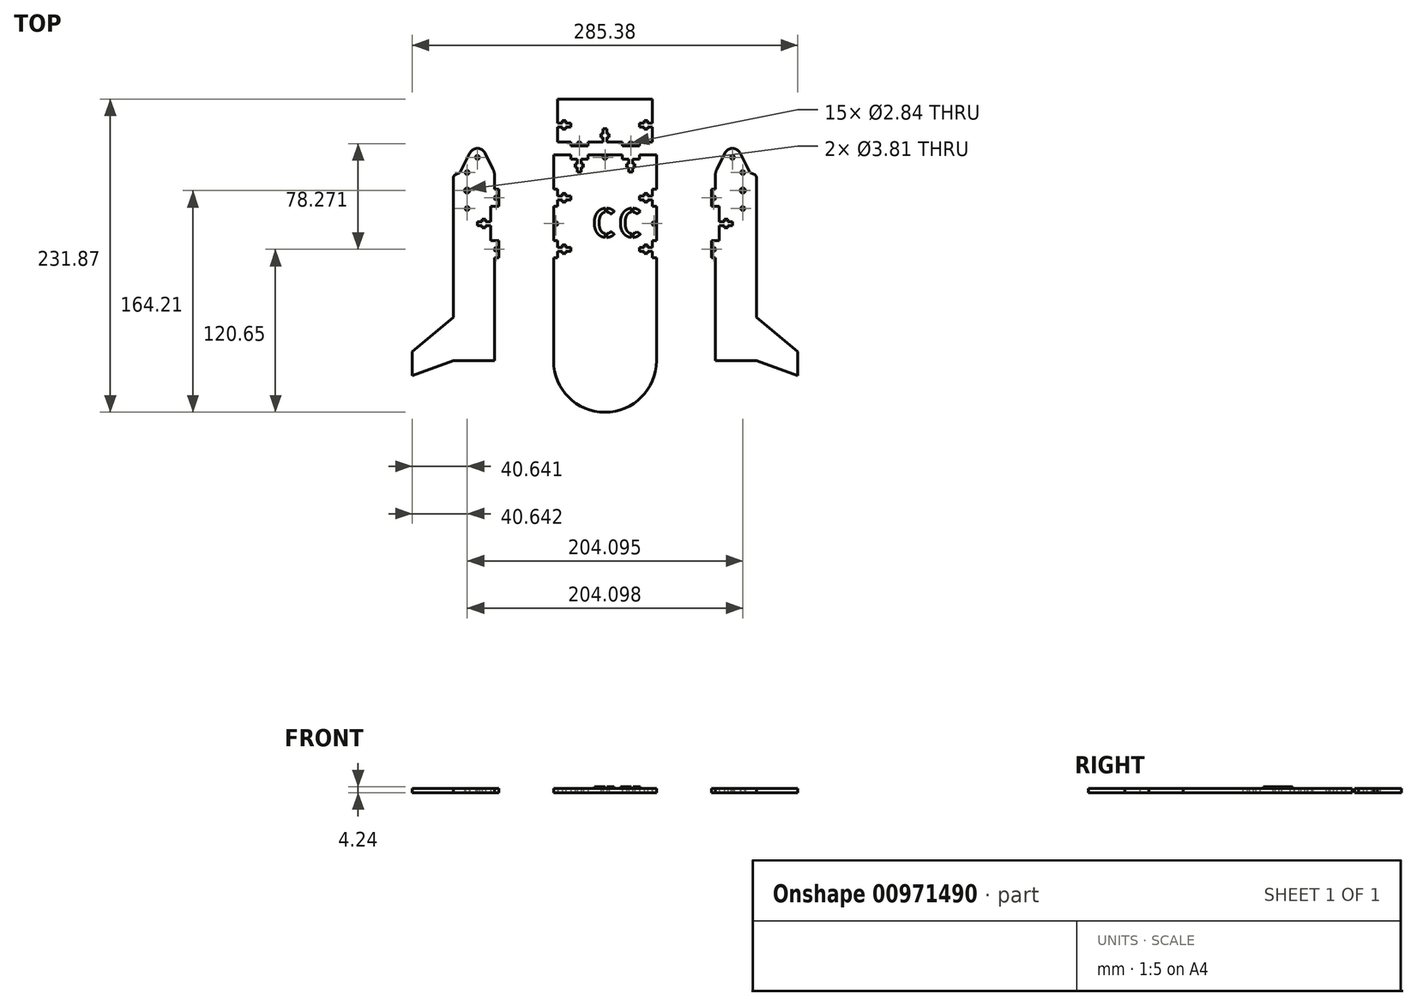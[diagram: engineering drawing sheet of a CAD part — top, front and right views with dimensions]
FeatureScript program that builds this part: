
annotation { "Feature Type Name" : "Feature", "Feature Type Description" : "" }
export const myFeature = defineFeature(function(context is Context, id is Id, definition is map)
    precondition{}
    {
        {
            var Q0;
            Q0=qCreatedBy(makeId("Top.planeOp"),FACE);
            var sketch = newSketch(context, id + "F0", { "sketchPlane" : qUnion([Q0])});
            skLineSegment(sketch, "E0", {"start": v(-12.7, 0) * mm, "end": v(12.7, 0) * mm});
            skLineSegment(sketch, "E1", {"start": v(-12.7, 0) * mm, "end": v(-12.7, -2.97) * mm});
            skLineSegment(sketch, "E2", {"start": v(-12.7, -2.97) * mm, "end": v(-17.63, -2.97) * mm});
            skLineSegment(sketch, "E3", {"start": v(-17.63, -9.1) * mm, "end": v(-17.63, -12.7) * mm});
            skLineSegment(sketch, "E4", {"start": v(-17.63, -12.7) * mm, "end": v(-20.47, -12.7) * mm});
            skLineSegment(sketch, "E5", {"start": v(-20.47, -12.7) * mm, "end": v(-20.47, -9.1) * mm});
            skLineSegment(sketch, "E6", {"start": v(-20.47, -6.57) * mm, "end": v(-20.47, -2.97) * mm});
            skLineSegment(sketch, "E7", {"start": v(-20.47, -2.97) * mm, "end": v(-25.4, -2.97) * mm});
            skLineSegment(sketch, "E8", {"start": v(-25.4, -2.97) * mm, "end": v(-25.4, 0) * mm});
            skCircle(sketch, "E9", {"center": v(0, -1.78) * mm, "radius": 1.42 * mm});
            skLineSegment(sketch, "E10", {"start": v(12.7, 0) * mm, "end": v(12.7, -2.97) * mm});
            skLineSegment(sketch, "E11", {"start": v(12.7, -2.97) * mm, "end": v(17.63, -2.97) * mm});
            skLineSegment(sketch, "E12", {"start": v(17.63, -2.97) * mm, "end": v(17.63, -6.57) * mm});
            skLineSegment(sketch, "E13", {"start": v(17.63, -9.1) * mm, "end": v(17.63, -12.7) * mm});
            skLineSegment(sketch, "E14", {"start": v(17.63, -12.7) * mm, "end": v(20.47, -12.7) * mm});
            skLineSegment(sketch, "E15", {"start": v(20.47, -12.7) * mm, "end": v(20.47, -9.1) * mm});
            skLineSegment(sketch, "E16", {"start": v(20.47, -6.57) * mm, "end": v(20.47, -2.97) * mm});
            skLineSegment(sketch, "E17", {"start": v(20.47, -2.97) * mm, "end": v(25.4, -2.97) * mm});
            skLineSegment(sketch, "E18", {"start": v(25.4, -2.97) * mm, "end": v(25.4, 0) * mm});
            skLineSegment(sketch, "E19", {"start": v(-38.1, 0) * mm, "end": v(-38.1, -25.4) * mm});
            skLineSegment(sketch, "E20", {"start": v(-38.1, -25.4) * mm, "end": v(-35.13, -25.4) * mm});
            skLineSegment(sketch, "E21", {"start": v(-35.13, -25.4) * mm, "end": v(-35.13, -30.33) * mm});
            skLineSegment(sketch, "E22", {"start": v(-35.13, -33.17) * mm, "end": v(-35.13, -38.1) * mm});
            skLineSegment(sketch, "E23", {"start": v(-35.13, -38.1) * mm, "end": v(-38.1, -38.1) * mm});
            skLineSegment(sketch, "E24", {"start": v(-25.4, 0) * mm, "end": v(-38.1, 0) * mm});
            skLineSegment(sketch, "E25", {"start": v(-20.47, -6.57) * mm, "end": v(-22.2, -6.57) * mm});
            skLineSegment(sketch, "E26", {"start": v(-22.2, -6.57) * mm, "end": v(-22.2, -9.1) * mm});
            skLineSegment(sketch, "E27", {"start": v(-22.2, -9.1) * mm, "end": v(-20.47, -9.1) * mm});
            skLineSegment(sketch, "E28", {"start": v(-17.63, -9.1) * mm, "end": v(-15.9, -9.1) * mm});
            skLineSegment(sketch, "E29", {"start": v(-15.9, -9.1) * mm, "end": v(-15.9, -6.57) * mm});
            skLineSegment(sketch, "E30", {"start": v(-15.9, -6.57) * mm, "end": v(-17.63, -6.57) * mm});
            skLineSegment(sketch, "E31", {"start": v(17.63, -6.57) * mm, "end": v(15.9, -6.57) * mm});
            skLineSegment(sketch, "E32", {"start": v(15.9, -6.57) * mm, "end": v(15.9, -9.1) * mm});
            skLineSegment(sketch, "E33", {"start": v(15.9, -9.1) * mm, "end": v(17.63, -9.1) * mm});
            skLineSegment(sketch, "E34", {"start": v(20.47, -9.1) * mm, "end": v(22.2, -9.1) * mm});
            skLineSegment(sketch, "E35", {"start": v(22.2, -9.1) * mm, "end": v(22.2, -6.57) * mm});
            skLineSegment(sketch, "E36", {"start": v(22.2, -6.57) * mm, "end": v(20.47, -6.57) * mm});
            skLineSegment(sketch, "E37", {"start": v(0, 0) * mm, "end": v(-12.7, 0) * mm, "construction": true});
            skLineSegment(sketch, "E38", {"start": v(0, 0) * mm, "end": v(12.7, 0) * mm, "construction": true});
            skLineSegment(sketch, "E39", {"start": v(-17.63, -6.57) * mm, "end": v(-17.63, -2.97) * mm});
            skLineSegment(sketch, "E40", {"start": v(-35.13, -30.33) * mm, "end": v(-31.53, -30.33) * mm});
            skLineSegment(sketch, "E41", {"start": v(-31.53, -30.33) * mm, "end": v(-31.53, -28.6) * mm});
            skLineSegment(sketch, "E42", {"start": v(-31.53, -28.6) * mm, "end": v(-29, -28.6) * mm});
            skLineSegment(sketch, "E43", {"start": v(-29, -28.6) * mm, "end": v(-29, -30.33) * mm});
            skLineSegment(sketch, "E44", {"start": v(-29, -30.33) * mm, "end": v(-25.4, -30.33) * mm});
            skLineSegment(sketch, "E45", {"start": v(-25.4, -30.33) * mm, "end": v(-25.4, -33.17) * mm});
            skLineSegment(sketch, "E46", {"start": v(-25.4, -33.17) * mm, "end": v(-29, -33.17) * mm});
            skLineSegment(sketch, "E47", {"start": v(-29, -33.17) * mm, "end": v(-29, -34.9) * mm});
            skLineSegment(sketch, "E48", {"start": v(-29, -34.9) * mm, "end": v(-31.53, -34.9) * mm});
            skLineSegment(sketch, "E49", {"start": v(-31.53, -34.9) * mm, "end": v(-31.53, -33.17) * mm});
            skLineSegment(sketch, "E50", {"start": v(-31.53, -33.17) * mm, "end": v(-35.13, -33.17) * mm});
            skLineSegment(sketch, "E51", {"start": v(-38.1, -38.1) * mm, "end": v(-38.1, -63.5) * mm});
            skCircle(sketch, "E52", {"center": v(-36.32, -50.8) * mm, "radius": 1.42 * mm});
            skLineSegment(sketch, "E53", {"start": v(-38.1, -63.5) * mm, "end": v(-35.13, -63.5) * mm});
            skLineSegment(sketch, "E54", {"start": v(-35.13, -63.5) * mm, "end": v(-35.13, -68.43) * mm});
            skLineSegment(sketch, "E55", {"start": v(-35.13, -68.43) * mm, "end": v(-31.53, -68.43) * mm});
            skLineSegment(sketch, "E56", {"start": v(-31.53, -68.43) * mm, "end": v(-31.53, -66.7) * mm});
            skLineSegment(sketch, "E57", {"start": v(-31.53, -66.7) * mm, "end": v(-29, -66.7) * mm});
            skLineSegment(sketch, "E58", {"start": v(-29, -66.7) * mm, "end": v(-29, -68.43) * mm});
            skLineSegment(sketch, "E59", {"start": v(-29, -68.43) * mm, "end": v(-25.4, -68.43) * mm});
            skLineSegment(sketch, "E60", {"start": v(-25.4, -68.43) * mm, "end": v(-25.4, -71.27) * mm});
            skLineSegment(sketch, "E61", {"start": v(-25.4, -71.27) * mm, "end": v(-29, -71.27) * mm});
            skLineSegment(sketch, "E62", {"start": v(-29, -71.27) * mm, "end": v(-29, -73) * mm});
            skLineSegment(sketch, "E63", {"start": v(-29, -73) * mm, "end": v(-31.53, -73) * mm});
            skLineSegment(sketch, "E64", {"start": v(-31.53, -73) * mm, "end": v(-31.53, -71.27) * mm});
            skLineSegment(sketch, "E65", {"start": v(-31.53, -71.27) * mm, "end": v(-35.13, -71.27) * mm});
            skLineSegment(sketch, "E66", {"start": v(-35.13, -71.27) * mm, "end": v(-35.13, -76.2) * mm});
            skLineSegment(sketch, "E67", {"start": v(-35.13, -76.2) * mm, "end": v(-38.1, -76.2) * mm});
            skLineSegment(sketch, "E68", {"start": v(-38.1, -76.2) * mm, "end": v(-38.1, -152.4) * mm});
            skLineSegment(sketch, "E69", {"start": v(0, -190.5) * mm, "end": v(0, -190.5) * mm});
            skPoint(sketch, "E70.visualSharp", {"position": v(-38.1, -190.5) * mm});
            skArc(sketch, "E70.filletArc", {"start": v(-38.1, -152.4) * mm, "mid": v(-26.94, -179.34) * mm, "end": v(0, -190.5) * mm});
            skPoint(sketch, "E71.visualSharp", {"position": v(38.1, -190.5) * mm});
            skLineSegment(sketch, "E72", {"start": v(0, -190.5) * mm, "end": v(0, -135.08) * mm, "construction": true});
            skArc(sketch, "E73.MirrorCS", {"start": v(38.1, -152.4) * mm, "mid": v(26.94, -179.34) * mm, "end": v(0, -190.5) * mm});
            skLineSegment(sketch, "E74.MirrorCS", {"start": v(38.1, -76.2) * mm, "end": v(38.1, -152.4) * mm});
            skLineSegment(sketch, "E75.MirrorCS", {"start": v(35.13, -76.2) * mm, "end": v(38.1, -76.2) * mm});
            skLineSegment(sketch, "E76.MirrorCS", {"start": v(35.13, -71.27) * mm, "end": v(35.13, -76.2) * mm});
            skLineSegment(sketch, "E77.MirrorCS", {"start": v(31.53, -71.27) * mm, "end": v(35.13, -71.27) * mm});
            skLineSegment(sketch, "E78.MirrorCS", {"start": v(31.53, -73) * mm, "end": v(31.53, -71.27) * mm});
            skLineSegment(sketch, "E79.MirrorCS", {"start": v(29, -73) * mm, "end": v(31.53, -73) * mm});
            skLineSegment(sketch, "E80.MirrorCS", {"start": v(29, -71.27) * mm, "end": v(29, -73) * mm});
            skLineSegment(sketch, "E81.MirrorCS", {"start": v(25.4, -71.27) * mm, "end": v(29, -71.27) * mm});
            skLineSegment(sketch, "E82.MirrorCS", {"start": v(25.4, -68.43) * mm, "end": v(25.4, -71.27) * mm});
            skLineSegment(sketch, "E83.MirrorCS", {"start": v(29, -68.43) * mm, "end": v(25.4, -68.43) * mm});
            skLineSegment(sketch, "E84.MirrorCS", {"start": v(29, -66.7) * mm, "end": v(29, -68.43) * mm});
            skLineSegment(sketch, "E85.MirrorCS", {"start": v(31.53, -66.7) * mm, "end": v(29, -66.7) * mm});
            skLineSegment(sketch, "E86.MirrorCS", {"start": v(31.53, -68.43) * mm, "end": v(31.53, -66.7) * mm});
            skLineSegment(sketch, "E87.MirrorCS", {"start": v(35.13, -68.43) * mm, "end": v(31.53, -68.43) * mm});
            skLineSegment(sketch, "E88.MirrorCS", {"start": v(35.13, -63.5) * mm, "end": v(35.13, -68.43) * mm});
            skLineSegment(sketch, "E89.MirrorCS", {"start": v(38.1, -63.5) * mm, "end": v(35.13, -63.5) * mm});
            skLineSegment(sketch, "E90.MirrorCS", {"start": v(38.1, -38.1) * mm, "end": v(38.1, -63.5) * mm});
            skCircle(sketch, "E91.MirrorC", {"center": v(36.32, -50.8) * mm, "radius": 1.42 * mm});
            skLineSegment(sketch, "E92.MirrorCS", {"start": v(35.13, -38.1) * mm, "end": v(38.1, -38.1) * mm});
            skLineSegment(sketch, "E93.MirrorCS", {"start": v(35.13, -33.17) * mm, "end": v(35.13, -38.1) * mm});
            skLineSegment(sketch, "E94.MirrorCS", {"start": v(31.53, -33.17) * mm, "end": v(35.13, -33.17) * mm});
            skLineSegment(sketch, "E95.MirrorCS", {"start": v(31.53, -34.9) * mm, "end": v(31.53, -33.17) * mm});
            skLineSegment(sketch, "E96.MirrorCS", {"start": v(29, -34.9) * mm, "end": v(31.53, -34.9) * mm});
            skLineSegment(sketch, "E97.MirrorCS", {"start": v(29, -33.17) * mm, "end": v(29, -34.9) * mm});
            skLineSegment(sketch, "E98.MirrorCS", {"start": v(25.4, -33.17) * mm, "end": v(29, -33.17) * mm});
            skLineSegment(sketch, "E99.MirrorCS", {"start": v(25.4, -30.33) * mm, "end": v(25.4, -33.17) * mm});
            skLineSegment(sketch, "E100.MirrorCS", {"start": v(29, -30.33) * mm, "end": v(25.4, -30.33) * mm});
            skLineSegment(sketch, "E101.MirrorCS", {"start": v(29, -28.6) * mm, "end": v(29, -30.33) * mm});
            skLineSegment(sketch, "E102.MirrorCS", {"start": v(31.53, -28.6) * mm, "end": v(29, -28.6) * mm});
            skLineSegment(sketch, "E103.MirrorCS", {"start": v(31.53, -30.33) * mm, "end": v(31.53, -28.6) * mm});
            skLineSegment(sketch, "E104.MirrorCS", {"start": v(35.13, -30.33) * mm, "end": v(31.53, -30.33) * mm});
            skLineSegment(sketch, "E105.MirrorCS", {"start": v(35.13, -25.4) * mm, "end": v(35.13, -30.33) * mm});
            skLineSegment(sketch, "E106.MirrorCS", {"start": v(38.1, -25.4) * mm, "end": v(35.13, -25.4) * mm});
            skLineSegment(sketch, "E107.MirrorCS", {"start": v(38.1, 0) * mm, "end": v(38.1, -25.4) * mm});
            skLineSegment(sketch, "E108.MirrorCS", {"start": v(25.4, 0) * mm, "end": v(38.1, 0) * mm});
            skLineSegment(sketch, "E109", {"start": v(-12.7, 0) * mm, "end": v(-12.7, 6.64) * mm, "construction": true});
            skLineSegment(sketch, "E110", {"start": v(-12.7, 6.64) * mm, "end": v(-12.7, 9.62) * mm});
            skLineSegment(sketch, "E111", {"start": v(-12.7, 9.62) * mm, "end": v(-1.42, 9.62) * mm});
            skLineSegment(sketch, "E112.MirrorCS", {"start": v(12.7, 9.62) * mm, "end": v(1.42, 9.62) * mm});
            skLineSegment(sketch, "E113.MirrorCS", {"start": v(12.7, 6.64) * mm, "end": v(12.7, 9.62) * mm});
            skLineSegment(sketch, "E114", {"start": v(-1.42, 9.62) * mm, "end": v(-1.42, 13.2) * mm});
            skLineSegment(sketch, "E115", {"start": v(-1.42, 13.2) * mm, "end": v(-3.15, 13.2) * mm});
            skLineSegment(sketch, "E116", {"start": v(-3.15, 13.2) * mm, "end": v(-3.15, 15.75) * mm});
            skLineSegment(sketch, "E117", {"start": v(-3.15, 15.75) * mm, "end": v(-1.42, 15.75) * mm});
            skLineSegment(sketch, "E118", {"start": v(-1.42, 15.75) * mm, "end": v(-1.42, 19.34) * mm});
            skLineSegment(sketch, "E119.MirrorCS", {"start": v(1.42, 9.62) * mm, "end": v(1.42, 13.2) * mm});
            skLineSegment(sketch, "E120.MirrorCS", {"start": v(1.42, 13.2) * mm, "end": v(3.15, 13.2) * mm});
            skLineSegment(sketch, "E121.MirrorCS", {"start": v(3.15, 13.2) * mm, "end": v(3.15, 15.75) * mm});
            skLineSegment(sketch, "E122.MirrorCS", {"start": v(3.15, 15.75) * mm, "end": v(1.42, 15.75) * mm});
            skLineSegment(sketch, "E123.MirrorCS", {"start": v(1.42, 15.75) * mm, "end": v(1.42, 19.34) * mm});
            skLineSegment(sketch, "E124", {"start": v(-1.42, 19.34) * mm, "end": v(1.42, 19.34) * mm});
            skLineSegment(sketch, "E125", {"start": v(12.7, 6.64) * mm, "end": v(25.4, 6.64) * mm});
            skLineSegment(sketch, "E126", {"start": v(-12.7, 6.64) * mm, "end": v(-25.4, 6.64) * mm});
            skCircle(sketch, "E127", {"center": v(-19.05, 8.42) * mm, "radius": 1.42 * mm});
            skLineSegment(sketch, "E128", {"start": v(25.4, 6.64) * mm, "end": v(25.4, 9.62) * mm});
            skCircle(sketch, "E129.MirrorC", {"center": v(19.05, 8.42) * mm, "radius": 1.42 * mm});
            skLineSegment(sketch, "E130.MirrorCS", {"start": v(-25.4, 6.64) * mm, "end": v(-25.4, 9.62) * mm});
            skLineSegment(sketch, "E131", {"start": v(35.13, 20.9) * mm, "end": v(31.53, 20.9) * mm});
            skLineSegment(sketch, "E132", {"start": v(31.53, 20.9) * mm, "end": v(31.53, 19.17) * mm});
            skLineSegment(sketch, "E133", {"start": v(31.53, 19.17) * mm, "end": v(29, 19.17) * mm});
            skLineSegment(sketch, "E134", {"start": v(29, 19.17) * mm, "end": v(29, 20.9) * mm});
            skLineSegment(sketch, "E135", {"start": v(29, 20.9) * mm, "end": v(25.4, 20.9) * mm});
            skLineSegment(sketch, "E136", {"start": v(25.4, 20.9) * mm, "end": v(25.4, 23.74) * mm});
            skLineSegment(sketch, "E137", {"start": v(25.4, 23.74) * mm, "end": v(29, 23.74) * mm});
            skLineSegment(sketch, "E138", {"start": v(29, 23.74) * mm, "end": v(29, 25.46) * mm});
            skLineSegment(sketch, "E139", {"start": v(29, 25.46) * mm, "end": v(31.53, 25.46) * mm});
            skLineSegment(sketch, "E140", {"start": v(31.53, 25.46) * mm, "end": v(31.53, 23.74) * mm});
            skLineSegment(sketch, "E141", {"start": v(31.53, 23.74) * mm, "end": v(35.13, 23.74) * mm});
            skLineSegment(sketch, "E142.MirrorCS", {"start": v(-35.13, 20.9) * mm, "end": v(-31.53, 20.9) * mm});
            skLineSegment(sketch, "E143.MirrorCS", {"start": v(-31.53, 20.9) * mm, "end": v(-31.53, 19.17) * mm});
            skLineSegment(sketch, "E144.MirrorCS", {"start": v(-31.53, 19.17) * mm, "end": v(-29, 19.17) * mm});
            skLineSegment(sketch, "E145.MirrorCS", {"start": v(-29, 19.17) * mm, "end": v(-29, 20.9) * mm});
            skLineSegment(sketch, "E146.MirrorCS", {"start": v(-29, 20.9) * mm, "end": v(-25.4, 20.9) * mm});
            skLineSegment(sketch, "E147.MirrorCS", {"start": v(-25.4, 20.9) * mm, "end": v(-25.4, 23.74) * mm});
            skLineSegment(sketch, "E148.MirrorCS", {"start": v(-25.4, 23.74) * mm, "end": v(-29, 23.74) * mm});
            skLineSegment(sketch, "E149.MirrorCS", {"start": v(-29, 23.74) * mm, "end": v(-29, 25.46) * mm});
            skLineSegment(sketch, "E150.MirrorCS", {"start": v(-29, 25.46) * mm, "end": v(-31.53, 25.46) * mm});
            skLineSegment(sketch, "E151.MirrorCS", {"start": v(-31.53, 25.46) * mm, "end": v(-31.53, 23.74) * mm});
            skLineSegment(sketch, "E152.MirrorCS", {"start": v(-31.53, 23.74) * mm, "end": v(-35.13, 23.74) * mm});
            skLineSegment(sketch, "E153", {"start": v(-38.1, 0) * mm, "end": v(-81.73, 0) * mm, "construction": true});
            skLineSegment(sketch, "E154", {"start": v(-81.73, 0) * mm, "end": v(-81.73, -12.7) * mm, "construction": true});
            skLineSegment(sketch, "E155", {"start": v(-81.73, -15.4) * mm, "end": v(-81.73, -25.36) * mm});
            skLineSegment(sketch, "E156", {"start": v(-82.94, -10.29) * mm, "end": v(-88.75, 1.34) * mm});
            skLineSegment(sketch, "E157", {"start": v(-100.1, 1.34) * mm, "end": v(-106.75, -11.94) * mm});
            skPoint(sketch, "E158.visualSharp", {"position": v(-81.73, -12.7) * mm});
            skArc(sketch, "E158.filletArc", {"start": v(-81.73, -15.4) * mm, "mid": v(-82.03, -12.77) * mm, "end": v(-82.94, -10.29) * mm});
            skPoint(sketch, "E159.visualSharp", {"position": v(-94.43, 12.7) * mm});
            skArc(sketch, "E159.filletArc", {"start": v(-88.75, 1.34) * mm, "mid": v(-94.43, 4.85) * mm, "end": v(-100.1, 1.34) * mm});
            skLineSegment(sketch, "E160", {"start": v(-107.89, -13.08) * mm, "end": v(-110.8, -14.54) * mm});
            skPoint(sketch, "E161.visualSharp", {"position": v(-107.13, -12.7) * mm});
            skArc(sketch, "E161.filletArc", {"start": v(-107.89, -13.08) * mm, "mid": v(-107.23, -12.6) * mm, "end": v(-106.75, -11.94) * mm});
            skLineSegment(sketch, "E162", {"start": v(-112.2, -16.8) * mm, "end": v(-112.2, -120.14) * mm});
            skPoint(sketch, "E163.visualSharp", {"position": v(-112.2, -15.24) * mm});
            skArc(sketch, "E163.filletArc", {"start": v(-110.8, -14.54) * mm, "mid": v(-111.83, -15.47) * mm, "end": v(-112.2, -16.8) * mm});
            skLineSegment(sketch, "E164", {"start": v(-112.2, -152.4) * mm, "end": v(-81.73, -152.4) * mm});
            skLineSegment(sketch, "E165", {"start": v(-112.2, -152.4) * mm, "end": v(-142.69, -163.5) * mm});
            skLineSegment(sketch, "E166", {"start": v(-142.69, -163.5) * mm, "end": v(-142.69, -145.71) * mm});
            skLineSegment(sketch, "E167", {"start": v(-142.69, -145.71) * mm, "end": v(-112.2, -120.14) * mm});
            skLineSegment(sketch, "E168", {"start": v(-81.73, 0) * mm, "end": v(-94.43, 0) * mm, "construction": true});
            skCircle(sketch, "E169", {"center": v(-94.43, -1.78) * mm, "radius": 1.42 * mm});
            skCircle(sketch, "E170", {"center": v(-80.54, -31.75) * mm, "radius": 1.42 * mm});
            skLineSegment(sketch, "E171", {"start": v(-81.73, -38.1) * mm, "end": v(-84.7, -38.1) * mm});
            skLineSegment(sketch, "E172", {"start": v(-84.7, -38.1) * mm, "end": v(-84.7, -49.38) * mm});
            skLineSegment(sketch, "E173", {"start": v(-84.7, -49.38) * mm, "end": v(-88.3, -49.38) * mm});
            skLineSegment(sketch, "E174", {"start": v(-88.3, -49.38) * mm, "end": v(-88.3, -47.65) * mm});
            skLineSegment(sketch, "E175", {"start": v(-88.3, -47.65) * mm, "end": v(-90.84, -47.65) * mm});
            skLineSegment(sketch, "E176", {"start": v(-90.84, -47.65) * mm, "end": v(-90.84, -49.38) * mm});
            skLineSegment(sketch, "E177", {"start": v(-90.84, -49.38) * mm, "end": v(-94.43, -49.38) * mm});
            skLineSegment(sketch, "E178", {"start": v(-94.43, -49.38) * mm, "end": v(-94.43, -52.22) * mm});
            skLineSegment(sketch, "E179", {"start": v(-94.43, -52.22) * mm, "end": v(-90.84, -52.22) * mm});
            skLineSegment(sketch, "E180", {"start": v(-90.84, -52.22) * mm, "end": v(-90.84, -53.95) * mm});
            skLineSegment(sketch, "E181", {"start": v(-90.84, -53.95) * mm, "end": v(-88.3, -53.95) * mm});
            skLineSegment(sketch, "E182", {"start": v(-88.3, -53.95) * mm, "end": v(-88.3, -52.22) * mm});
            skLineSegment(sketch, "E183", {"start": v(-88.3, -52.22) * mm, "end": v(-84.7, -52.22) * mm});
            skLineSegment(sketch, "E184", {"start": v(-84.7, -52.22) * mm, "end": v(-84.7, -63.5) * mm});
            skLineSegment(sketch, "E185", {"start": v(-84.7, -63.5) * mm, "end": v(-81.73, -63.5) * mm});
            skLineSegment(sketch, "E186.trimOffspring", {"start": v(-81.73, -76.2) * mm, "end": v(-81.73, -152.4) * mm});
            skCircle(sketch, "E187", {"center": v(-80.54, -69.85) * mm, "radius": 1.42 * mm});
            skCircle(sketch, "E188", {"center": v(-102.05, -12.96) * mm, "radius": 1.42 * mm});
            skCircle(sketch, "E189", {"center": v(-102.05, -26.3) * mm, "radius": 1.9 * mm});
            skLineSegment(sketch, "E190", {"start": v(-102.05, -12.96) * mm, "end": v(-81.73, -12.7) * mm, "construction": true});
            skLineSegment(sketch, "E191", {"start": v(-102.05, -26.3) * mm, "end": v(-81.73, -26.3) * mm, "construction": true});
            skCircle(sketch, "E192.MirrorC", {"center": v(-102.05, -39.63) * mm, "radius": 1.42 * mm});
            skLineSegment(sketch, "E193.MirrorCS", {"start": v(81.73, -76.2) * mm, "end": v(81.73, -152.4) * mm});
            skLineSegment(sketch, "E194.MirrorCS", {"start": v(112.2, -152.4) * mm, "end": v(81.73, -152.4) * mm});
            skLineSegment(sketch, "E195.MirrorCS", {"start": v(112.2, -152.4) * mm, "end": v(142.69, -163.5) * mm});
            skLineSegment(sketch, "E196.MirrorCS", {"start": v(142.69, -163.5) * mm, "end": v(142.69, -145.71) * mm});
            skLineSegment(sketch, "E197.MirrorCS", {"start": v(142.69, -145.71) * mm, "end": v(112.2, -120.14) * mm});
            skLineSegment(sketch, "E198.MirrorCS", {"start": v(112.2, -16.8) * mm, "end": v(112.2, -120.14) * mm});
            skArc(sketch, "E199.MirrorCS", {"start": v(110.8, -14.54) * mm, "mid": v(111.83, -15.47) * mm, "end": v(112.2, -16.8) * mm});
            skLineSegment(sketch, "E200.MirrorCS", {"start": v(107.89, -13.08) * mm, "end": v(110.8, -14.54) * mm});
            skArc(sketch, "E201.MirrorCS", {"start": v(107.89, -13.08) * mm, "mid": v(107.23, -12.6) * mm, "end": v(106.75, -11.94) * mm});
            skLineSegment(sketch, "E202.MirrorCS", {"start": v(100.1, 1.34) * mm, "end": v(106.75, -11.94) * mm});
            skArc(sketch, "E203.MirrorCS", {"start": v(88.75, 1.34) * mm, "mid": v(94.43, 4.85) * mm, "end": v(100.1, 1.34) * mm});
            skLineSegment(sketch, "E204.MirrorCS", {"start": v(82.94, -10.29) * mm, "end": v(88.75, 1.34) * mm});
            skArc(sketch, "E205.MirrorCS", {"start": v(81.73, -15.4) * mm, "mid": v(82.03, -12.77) * mm, "end": v(82.94, -10.29) * mm});
            skLineSegment(sketch, "E206.MirrorCS", {"start": v(81.73, -15.4) * mm, "end": v(81.73, -25.36) * mm});
            skCircle(sketch, "E207.MirrorC", {"center": v(80.54, -69.85) * mm, "radius": 1.42 * mm});
            skCircle(sketch, "E208.MirrorC", {"center": v(80.54, -31.75) * mm, "radius": 1.42 * mm});
            skLineSegment(sketch, "E209.MirrorCS", {"start": v(81.73, -38.1) * mm, "end": v(84.7, -38.1) * mm});
            skLineSegment(sketch, "E210.MirrorCS", {"start": v(84.7, -38.1) * mm, "end": v(84.7, -49.38) * mm});
            skLineSegment(sketch, "E211.MirrorCS", {"start": v(84.7, -52.22) * mm, "end": v(84.7, -63.5) * mm});
            skLineSegment(sketch, "E212.MirrorCS", {"start": v(84.7, -63.5) * mm, "end": v(81.73, -63.5) * mm});
            skLineSegment(sketch, "E213.MirrorCS", {"start": v(88.3, -52.22) * mm, "end": v(84.7, -52.22) * mm});
            skLineSegment(sketch, "E214.MirrorCS", {"start": v(84.7, -49.38) * mm, "end": v(88.3, -49.38) * mm});
            skLineSegment(sketch, "E215.MirrorCS", {"start": v(88.3, -49.38) * mm, "end": v(88.3, -47.65) * mm});
            skLineSegment(sketch, "E216.MirrorCS", {"start": v(88.3, -47.65) * mm, "end": v(90.84, -47.65) * mm});
            skLineSegment(sketch, "E217.MirrorCS", {"start": v(90.84, -47.65) * mm, "end": v(90.84, -49.38) * mm});
            skLineSegment(sketch, "E218.MirrorCS", {"start": v(90.84, -49.38) * mm, "end": v(94.43, -49.38) * mm});
            skLineSegment(sketch, "E219.MirrorCS", {"start": v(94.43, -49.38) * mm, "end": v(94.43, -52.22) * mm});
            skLineSegment(sketch, "E220.MirrorCS", {"start": v(94.43, -52.22) * mm, "end": v(90.84, -52.22) * mm});
            skLineSegment(sketch, "E221.MirrorCS", {"start": v(90.84, -52.22) * mm, "end": v(90.84, -53.95) * mm});
            skLineSegment(sketch, "E222.MirrorCS", {"start": v(90.84, -53.95) * mm, "end": v(88.3, -53.95) * mm});
            skLineSegment(sketch, "E223.MirrorCS", {"start": v(88.3, -53.95) * mm, "end": v(88.3, -52.22) * mm});
            skCircle(sketch, "E224.MirrorC", {"center": v(94.43, -1.78) * mm, "radius": 1.42 * mm});
            skCircle(sketch, "E225.MirrorC", {"center": v(102.05, -12.96) * mm, "radius": 1.42 * mm});
            skCircle(sketch, "E226.MirrorC", {"center": v(102.05, -26.3) * mm, "radius": 1.9 * mm});
            skCircle(sketch, "E227.MirrorC", {"center": v(102.05, -39.63) * mm, "radius": 1.42 * mm});
            skLineSegment(sketch, "E228", {"start": v(-25.4, 9.62) * mm, "end": v(-35.13, 9.62) * mm});
            skLineSegment(sketch, "E229", {"start": v(-35.13, 9.62) * mm, "end": v(-35.13, 20.9) * mm});
            skLineSegment(sketch, "E230", {"start": v(25.4, 9.62) * mm, "end": v(35.13, 9.62) * mm});
            skLineSegment(sketch, "E231", {"start": v(35.13, 9.62) * mm, "end": v(35.13, 20.9) * mm});
            skLineSegment(sketch, "E232", {"start": v(-35.13, 23.74) * mm, "end": v(-35.13, 41.37) * mm});
            skLineSegment(sketch, "E233", {"start": v(35.13, 23.74) * mm, "end": v(35.13, 41.37) * mm});
            skLineSegment(sketch, "E234", {"start": v(-35.13, 41.37) * mm, "end": v(35.13, 41.37) * mm});
            skLineSegment(sketch, "E235", {"start": v(-81.73, -38.1) * mm, "end": v(-78.76, -38.06) * mm});
            skLineSegment(sketch, "E236", {"start": v(-78.76, -38.06) * mm, "end": v(-78.76, -25.36) * mm});
            skLineSegment(sketch, "E237", {"start": v(-78.76, -25.36) * mm, "end": v(-81.73, -25.36) * mm});
            skLineSegment(sketch, "E238", {"start": v(-81.73, -63.5) * mm, "end": v(-78.76, -63.5) * mm});
            skLineSegment(sketch, "E239", {"start": v(-78.76, -63.5) * mm, "end": v(-78.76, -76.2) * mm});
            skLineSegment(sketch, "E240", {"start": v(-78.76, -76.2) * mm, "end": v(-81.73, -76.2) * mm});
            skLineSegment(sketch, "E241.MirrorCS", {"start": v(78.76, -25.36) * mm, "end": v(81.73, -25.36) * mm});
            skLineSegment(sketch, "E242.MirrorCS", {"start": v(78.76, -38.06) * mm, "end": v(78.76, -25.36) * mm});
            skLineSegment(sketch, "E243.MirrorCS", {"start": v(81.73, -38.1) * mm, "end": v(78.76, -38.06) * mm});
            skLineSegment(sketch, "E244.MirrorCS", {"start": v(81.73, -63.5) * mm, "end": v(78.76, -63.5) * mm});
            skLineSegment(sketch, "E245.MirrorCS", {"start": v(78.76, -63.5) * mm, "end": v(78.76, -76.2) * mm});
            skLineSegment(sketch, "E246.MirrorCS", {"start": v(78.76, -76.2) * mm, "end": v(81.73, -76.2) * mm});
            skPoint(sketch, "E247.trimOffspring.end.orphan", {"position": v(81.73, -38.1) * mm});
            skPoint(sketch, "E248.orphan", {"position": v(81.73, -63.5) * mm});
            skSolve(sketch);
        }
        {
            var Q0;
            Q0 = qSketchRegion(id + "F0", true);
            extrude(context, id + "F1", {"entities" : qUnion([Q0]), "depth" : 2.97 * mm, "offsetDistance" : 25.4 * mm});
        }
        {
            var Q0;
            Q0=makeQuery(id+"F1.opExtrude","CAP_FACE",FACE,{"disambiguationData":[OSD([sQuery(id+"F0.wireOp",EDGE,"E0"),sQuery(id+"F0.wireOp",EDGE,"E1"),sQuery(id+"F0.wireOp",EDGE,"E2"),sQuery(id+"F0.wireOp",EDGE,"E3"),sQuery(id+"F0.wireOp",EDGE,"E4"),sQuery(id+"F0.wireOp",EDGE,"E5"),sQuery(id+"F0.wireOp",EDGE,"E6"),sQuery(id+"F0.wireOp",EDGE,"E7"),sQuery(id+"F0.wireOp",EDGE,"E8"),sQuery(id+"F0.wireOp",EDGE,"E9"),sQuery(id+"F0.wireOp",EDGE,"E10"),sQuery(id+"F0.wireOp",EDGE,"E11"),sQuery(id+"F0.wireOp",EDGE,"E12"),sQuery(id+"F0.wireOp",EDGE,"E13"),sQuery(id+"F0.wireOp",EDGE,"E14"),sQuery(id+"F0.wireOp",EDGE,"E15"),sQuery(id+"F0.wireOp",EDGE,"E16"),sQuery(id+"F0.wireOp",EDGE,"E17"),sQuery(id+"F0.wireOp",EDGE,"E18"),sQuery(id+"F0.wireOp",EDGE,"E19"),sQuery(id+"F0.wireOp",EDGE,"E20"),sQuery(id+"F0.wireOp",EDGE,"E21"),sQuery(id+"F0.wireOp",EDGE,"E22"),sQuery(id+"F0.wireOp",EDGE,"E23"),sQuery(id+"F0.wireOp",EDGE,"E24"),sQuery(id+"F0.wireOp",EDGE,"E25"),sQuery(id+"F0.wireOp",EDGE,"E26"),sQuery(id+"F0.wireOp",EDGE,"E27"),sQuery(id+"F0.wireOp",EDGE,"E28"),sQuery(id+"F0.wireOp",EDGE,"E29"),sQuery(id+"F0.wireOp",EDGE,"E30"),sQuery(id+"F0.wireOp",EDGE,"E31"),sQuery(id+"F0.wireOp",EDGE,"E32"),sQuery(id+"F0.wireOp",EDGE,"E33"),sQuery(id+"F0.wireOp",EDGE,"E34"),sQuery(id+"F0.wireOp",EDGE,"E35"),sQuery(id+"F0.wireOp",EDGE,"E36"),sQuery(id+"F0.wireOp",EDGE,"E39"),sQuery(id+"F0.wireOp",EDGE,"E40"),sQuery(id+"F0.wireOp",EDGE,"E41"),sQuery(id+"F0.wireOp",EDGE,"E42"),sQuery(id+"F0.wireOp",EDGE,"E43"),sQuery(id+"F0.wireOp",EDGE,"E44"),sQuery(id+"F0.wireOp",EDGE,"E45"),sQuery(id+"F0.wireOp",EDGE,"E46"),sQuery(id+"F0.wireOp",EDGE,"E47"),sQuery(id+"F0.wireOp",EDGE,"E48"),sQuery(id+"F0.wireOp",EDGE,"E49"),sQuery(id+"F0.wireOp",EDGE,"E50"),sQuery(id+"F0.wireOp",EDGE,"E51"),sQuery(id+"F0.wireOp",EDGE,"E52"),sQuery(id+"F0.wireOp",EDGE,"E53"),sQuery(id+"F0.wireOp",EDGE,"E54"),sQuery(id+"F0.wireOp",EDGE,"E55"),sQuery(id+"F0.wireOp",EDGE,"E56"),sQuery(id+"F0.wireOp",EDGE,"E57"),sQuery(id+"F0.wireOp",EDGE,"E58"),sQuery(id+"F0.wireOp",EDGE,"E59"),sQuery(id+"F0.wireOp",EDGE,"E60"),sQuery(id+"F0.wireOp",EDGE,"E61"),sQuery(id+"F0.wireOp",EDGE,"E62"),sQuery(id+"F0.wireOp",EDGE,"E63"),sQuery(id+"F0.wireOp",EDGE,"E64"),sQuery(id+"F0.wireOp",EDGE,"E65"),sQuery(id+"F0.wireOp",EDGE,"E66"),sQuery(id+"F0.wireOp",EDGE,"E67"),sQuery(id+"F0.wireOp",EDGE,"E68"),sQuery(id+"F0.wireOp",EDGE,"E70.filletArc"),sQuery(id+"F0.wireOp",EDGE,"E73.MirrorCS"),sQuery(id+"F0.wireOp",EDGE,"E74.MirrorCS"),sQuery(id+"F0.wireOp",EDGE,"E75.MirrorCS"),sQuery(id+"F0.wireOp",EDGE,"E76.MirrorCS"),sQuery(id+"F0.wireOp",EDGE,"E77.MirrorCS"),sQuery(id+"F0.wireOp",EDGE,"E78.MirrorCS"),sQuery(id+"F0.wireOp",EDGE,"E79.MirrorCS"),sQuery(id+"F0.wireOp",EDGE,"E80.MirrorCS"),sQuery(id+"F0.wireOp",EDGE,"E81.MirrorCS"),sQuery(id+"F0.wireOp",EDGE,"E82.MirrorCS"),sQuery(id+"F0.wireOp",EDGE,"E83.MirrorCS"),sQuery(id+"F0.wireOp",EDGE,"E84.MirrorCS"),sQuery(id+"F0.wireOp",EDGE,"E85.MirrorCS"),sQuery(id+"F0.wireOp",EDGE,"E86.MirrorCS"),sQuery(id+"F0.wireOp",EDGE,"E87.MirrorCS"),sQuery(id+"F0.wireOp",EDGE,"E88.MirrorCS"),sQuery(id+"F0.wireOp",EDGE,"E89.MirrorCS"),sQuery(id+"F0.wireOp",EDGE,"E90.MirrorCS"),sQuery(id+"F0.wireOp",EDGE,"E91.MirrorC"),sQuery(id+"F0.wireOp",EDGE,"E92.MirrorCS"),sQuery(id+"F0.wireOp",EDGE,"E93.MirrorCS"),sQuery(id+"F0.wireOp",EDGE,"E94.MirrorCS"),sQuery(id+"F0.wireOp",EDGE,"E95.MirrorCS"),sQuery(id+"F0.wireOp",EDGE,"E96.MirrorCS"),sQuery(id+"F0.wireOp",EDGE,"E97.MirrorCS"),sQuery(id+"F0.wireOp",EDGE,"E98.MirrorCS"),sQuery(id+"F0.wireOp",EDGE,"E99.MirrorCS"),sQuery(id+"F0.wireOp",EDGE,"E100.MirrorCS"),sQuery(id+"F0.wireOp",EDGE,"E101.MirrorCS"),sQuery(id+"F0.wireOp",EDGE,"E102.MirrorCS"),sQuery(id+"F0.wireOp",EDGE,"E103.MirrorCS"),sQuery(id+"F0.wireOp",EDGE,"E104.MirrorCS"),sQuery(id+"F0.wireOp",EDGE,"E105.MirrorCS"),sQuery(id+"F0.wireOp",EDGE,"E106.MirrorCS"),sQuery(id+"F0.wireOp",EDGE,"E107.MirrorCS"),sQuery(id+"F0.wireOp",EDGE,"E108.MirrorCS")])],"isStart":false});
            var sketch = newSketch(context, id + "F2", { "sketchPlane" : qUnion([Q0])});
            skText(sketch, "E249", { "text": "CC", "fontName": "AllertaStencil-Regular.ttf"});
            const initialGuessF2  = {"E249": [-0.01015, -0.06088, 1, 0, 0.0212]};
            skSetInitialGuess(sketch, initialGuessF2);
            skSolve(sketch);
        }
        {
            var Q0;
            Q0 = qSketchRegion(id + "F2", true);
            extrude(context, id + "F3", {"entities" : qUnion([Q0]), "operationType" : NewBodyOperationType.ADD, "depth" : 1.27 * mm, "offsetDistance" : 25.4 * mm});
        }
    });
